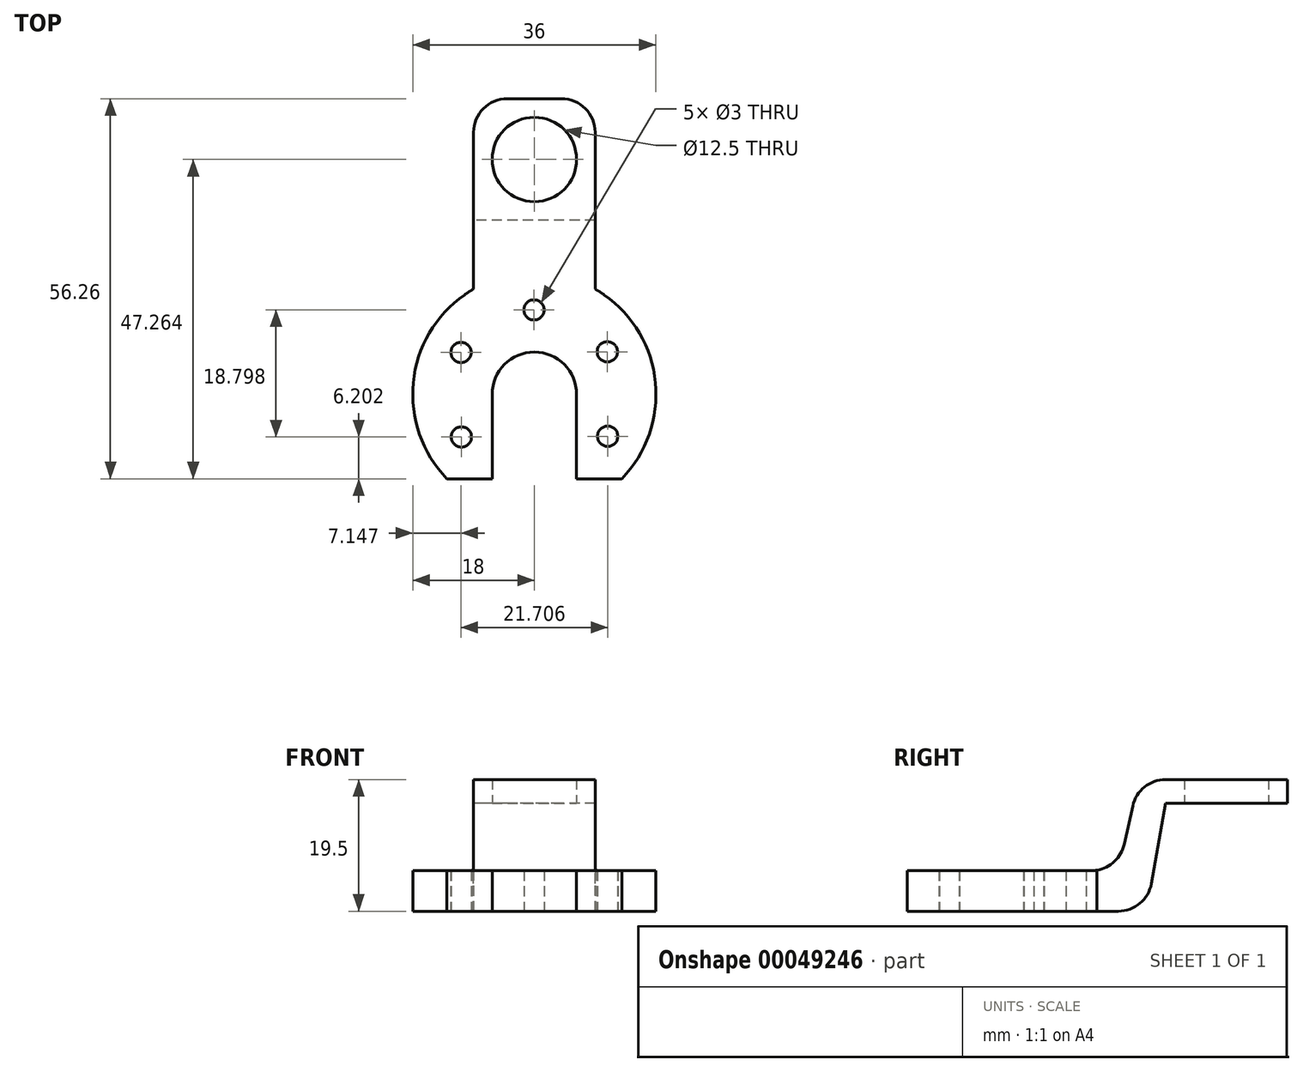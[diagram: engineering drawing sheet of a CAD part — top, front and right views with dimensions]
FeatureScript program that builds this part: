
annotation { "Feature Type Name" : "Feature", "Feature Type Description" : "" }
export const myFeature = defineFeature(function(context is Context, id is Id, definition is map)
    precondition{}
    {
        {
            var Q0;
            Q0=qCreatedBy(makeId("Top.planeOp"),FACE);
            var sketch = newSketch(context, id + "F0", { "sketchPlane" : qUnion([Q0])});
            skArc(sketch, "E0", {"start": v(12.95, -12.5) * mm, "mid": v(0, 18) * mm, "end": v(-12.95, -12.5) * mm});
            skCircle(sketch, "E1.cCircle", {"center": v(0, 0) * mm, "radius": 10.83 * mm, "construction": true});
            skLineSegment(sketch, "E1.0", {"start": v(-10.85, 6.2) * mm, "end": v(-0.06, 12.5) * mm, "construction": true});
            skLineSegment(sketch, "E1.1", {"start": v(-0.06, 12.5) * mm, "end": v(10.8, 6.3) * mm, "construction": true});
            skLineSegment(sketch, "E1.2", {"start": v(10.8, 6.3) * mm, "end": v(10.85, -6.2) * mm, "construction": true});
            skLineSegment(sketch, "E1.3", {"start": v(10.85, -6.2) * mm, "end": v(0.06, -12.5) * mm, "construction": true});
            skLineSegment(sketch, "E1.4", {"start": v(0.06, -12.5) * mm, "end": v(-10.8, -6.3) * mm, "construction": true});
            skLineSegment(sketch, "E1.5", {"start": v(-10.8, -6.3) * mm, "end": v(-10.85, 6.2) * mm, "construction": true});
            skPoint(sketch, "E1.0.midPoint", {"position": v(-5.45, 9.35) * mm});
            skArc(sketch, "E2", {"start": v(6.25, 0) * mm, "mid": v(0, 6.25) * mm, "end": v(-6.25, 0) * mm});
            skLineSegment(sketch, "E3", {"start": v(-6.25, 0) * mm, "end": v(-6.25, -12.5) * mm});
            skLineSegment(sketch, "E4", {"start": v(6.25, 0) * mm, "end": v(6.25, -12.5) * mm});
            skLineSegment(sketch, "E5", {"start": v(12.95, -12.5) * mm, "end": v(6.25, -12.5) * mm});
            skLineSegment(sketch, "E6.trimOffspring", {"start": v(-6.25, -12.5) * mm, "end": v(-12.95, -12.5) * mm});
            skSolve(sketch);
        }
        {
            var Q0;
            Q0=makeQuery(id+"F0.imprint","IMPRINT",FACE,{"disambiguationData":[TD([[makeQuery(id+"F0.imprint","IMPRINT",EDGE,{"derivedFrom":sQuery(id+"F0.wireOp",EDGE,"E0")}),1.0]])]});
            extrude(context, id + "F1", {"entities" : qUnion([Q0]), "depth" : 6 * mm});
        }
        {
            var Q0;
            Q0=qCreatedBy(makeId("Right.planeOp"),FACE);
            var sketch = newSketch(context, id + "F2", { "sketchPlane" : qUnion([Q0])});
            skLineSegment(sketch, "E7", {"start": v(22.93, 0) * mm, "end": v(25.76, 16) * mm});
            skLineSegment(sketch, "E8", {"start": v(25.76, 16) * mm, "end": v(43.76, 16) * mm});
            skLineSegment(sketch, "E9", {"start": v(43.76, 16) * mm, "end": v(43.76, 19.5) * mm});
            skLineSegment(sketch, "E10", {"start": v(43.76, 19.5) * mm, "end": v(21.76, 19.5) * mm});
            skLineSegment(sketch, "E11", {"start": v(21.76, 19.5) * mm, "end": v(18.76, 6) * mm});
            skLineSegment(sketch, "E12", {"start": v(25.76, 16) * mm, "end": v(25.76, 0) * mm, "construction": true});
            skLineSegment(sketch, "E13", {"start": v(43.76, 16) * mm, "end": v(43.76, -0.7) * mm, "construction": true});
            skLineSegment(sketch, "E14", {"start": v(18.76, 6) * mm, "end": v(18.76, 0.47) * mm, "construction": true});
            skLineSegment(sketch, "E15.bottom", {"start": v(27.65, 19.5) * mm, "end": v(40.15, 19.5) * mm, "construction": true});
            skLineSegment(sketch, "E15.top", {"start": v(27.65, 16) * mm, "end": v(40.15, 16) * mm, "construction": true});
            skLineSegment(sketch, "E15.left", {"start": v(27.65, 19.5) * mm, "end": v(27.65, 16) * mm, "construction": true});
            skLineSegment(sketch, "E15.right", {"start": v(40.15, 19.5) * mm, "end": v(40.15, 16) * mm, "construction": true});
            skPoint(sketch, "E16.end.orphan", {"position": v(1.98, 0) * mm});
            skLineSegment(sketch, "E17", {"start": v(22.93, 0) * mm, "end": v(11, 0) * mm});
            skLineSegment(sketch, "E18", {"start": v(11, 0) * mm, "end": v(11, 6) * mm});
            skLineSegment(sketch, "E19", {"start": v(11, 6) * mm, "end": v(18.76, 6) * mm});
            skSolve(sketch);
        }
        {
            var Q0;
            Q0=makeQuery(id+"F2.imprint","IMPRINT",FACE,{"disambiguationData":[TD([[makeQuery(id+"F2.imprint","IMPRINT",EDGE,{"derivedFrom":sQuery(id+"F2.wireOp",EDGE,"E7")}),1.0]])]});
            extrude(context, id + "F3", {"entities" : qUnion([Q0]), "operationType" : NewBodyOperationType.ADD, "depth" : 9 * mm, "hasSecondDirection" : true, "secondDirectionOppositeDirection" : true, "secondDirectionDepth" : 9 * mm});
        }
        {
            var Q0;
            Q0=makeQuery(id+"F3.opExtrude","SWEPT_FACE",FACE,{"disambiguationData":[OSD([sQuery(id+"F2.wireOp",EDGE,"E8")])]});
            var sketch = newSketch(context, id + "F4", { "sketchPlane" : qUnion([Q0])});
            skLineSegment(sketch, "E20", {"start": v(0, -43.76) * mm, "end": v(0, -41.01) * mm, "construction": true});
            skPoint(sketch, "E21", {"position": v(0, -34.76) * mm});
            skCircle(sketch, "E22", {"center": v(0, -34.76) * mm, "radius": 6.25 * mm});
            skLineSegment(sketch, "E23.trimOffspring", {"start": v(0, -28.51) * mm, "end": v(0, -25.76) * mm, "construction": true});
            skSolve(sketch);
        }
        {
            var Q0;
            Q0=makeQuery(id+"F4.imprint","IMPRINT",FACE,{"disambiguationData":[TD([[makeQuery(id+"F4.imprint","IMPRINT",EDGE,{"derivedFrom":sQuery(id+"F4.wireOp",EDGE,"E22")}),1.0]])]});
            extrude(context, id + "F5", {"entities" : qUnion([Q0]), "operationType" : NewBodyOperationType.REMOVE, "oppositeDirection" : true, "depth" : 25 * mm});
        }
        {
            var Q0;
            Q0=sQuery(id+"F0.wireOp",VERTEX,"E1.2.start");
            var Q1;
            Q1=sQuery(id+"F0.wireOp",VERTEX,"E1.3.start");
            var Q2;
            Q2=sQuery(id+"F0.wireOp",VERTEX,"E1.1.start");
            var Q3;
            Q3=sQuery(id+"F0.wireOp",VERTEX,"E1.5.end");
            var Q4;
            Q4=sQuery(id+"F0.wireOp",VERTEX,"E1.5.start");
            var Q5;
            Q5=makeQuery(id+"F1.opExtrude","SWEPT_BODY",BODY,{"disambiguationData":[OSD([sQuery(id+"F0.wireOp",EDGE,"E0"),sQuery(id+"F0.wireOp",EDGE,"E2"),sQuery(id+"F0.wireOp",EDGE,"E3"),sQuery(id+"F0.wireOp",EDGE,"E4"),sQuery(id+"F0.wireOp",EDGE,"E5"),sQuery(id+"F0.wireOp",EDGE,"E6.trimOffspring")])]});
            hole(context, id + "F6", {"style" : HoleStyle.SIMPLE, "endStyle" : HoleEndStyle.THROUGH, "oppositeDirection" : true, "holeDiameter" : 3 * mm, "locations" : qUnion([Q0, Q1, Q2, Q3, Q4]), "scope" : qUnion([Q5]), "isTappedThrough" : true});
        }
        {
            var Q0;
            Q0=makeQuery(id+"F3.opExtrude","SWEPT_EDGE",EDGE,{"disambiguationData":[OSD([sQuery(id+"F2.wireOp",EDGE,"E11"),sQuery(id+"F2.wireOp",EDGE,"E19")])]});
            var Q1;
            Q1=makeQuery(id+"F3.opExtrude","SWEPT_EDGE",EDGE,{"disambiguationData":[OSD([sQuery(id+"F2.wireOp",EDGE,"E10"),sQuery(id+"F2.wireOp",EDGE,"E11")])]});
            var Q2;
            Q2=makeQuery(id+"F3.opExtrude","SWEPT_EDGE",EDGE,{"disambiguationData":[OSD([sQuery(id+"F2.wireOp",EDGE,"E7"),sQuery(id+"F2.wireOp",EDGE,"E17")])]});
            var Q3;
            Q3=makeQuery(id+"F3.opExtrude","CAP_EDGE",EDGE,{"disambiguationData":[OSD([sQuery(id+"F2.wireOp",EDGE,"E9")])],"isStart":true});
            var Q4;
            Q4=makeQuery(id+"F3.opExtrude","CAP_EDGE",EDGE,{"disambiguationData":[OSD([sQuery(id+"F2.wireOp",EDGE,"E9")])],"isStart":false});
            fillet(context, id + "F7", {"entities" : qUnion([Q0, Q1, Q2, Q3, Q4]), "radius" : 5 * mm, "tangentPropagation" : true, "allowEdgeOverflow" : false});
        }
    });
